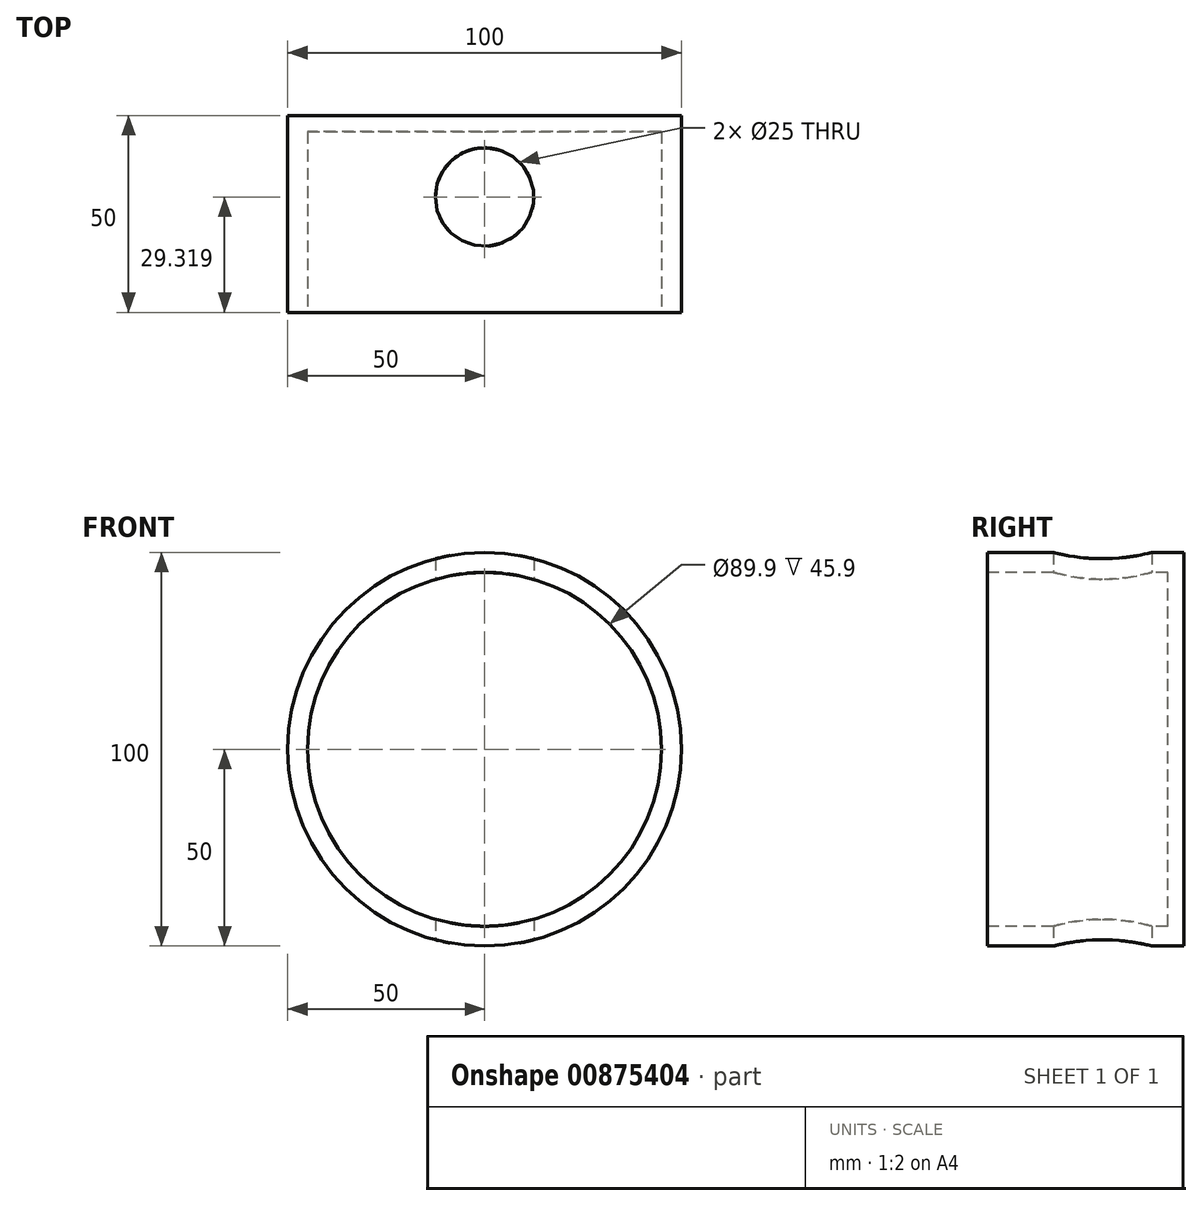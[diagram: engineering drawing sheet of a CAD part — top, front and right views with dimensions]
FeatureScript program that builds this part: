
annotation { "Feature Type Name" : "Feature", "Feature Type Description" : "" }
export const myFeature = defineFeature(function(context is Context, id is Id, definition is map)
    precondition{}
    {
        {
            var Q0;
            Q0=qCreatedBy(makeId("Front.planeOp"),FACE);
            var sketch = newSketch(context, id + "F0", { "sketchPlane" : qUnion([Q0])});
            skCircle(sketch, "E0", {"center": v(0, 0) * mm, "radius": 50 * mm});
            skSolve(sketch);
        }
        {
            var Q0;
            Q0 = qSketchRegion(id + "F0", true);
            extrude(context, id + "F1", {"entities" : qUnion([Q0]), "oppositeDirection" : true, "depth" : 50 * mm, "offsetDistance" : 25 * mm});
        }
        {
            var Q0;
            Q0=qCreatedBy(makeId("Top.planeOp"),FACE);
            var sketch = newSketch(context, id + "F2", { "sketchPlane" : qUnion([Q0])});
            skCircle(sketch, "E1", {"center": v(0, 29.32) * mm, "radius": 12.5 * mm});
            skSolve(sketch);
        }
        {
            var Q0;
            Q0 = qSketchRegion(id + "F2", true);
            extrude(context, id + "F3", {"entities" : qUnion([Q0]), "operationType" : NewBodyOperationType.REMOVE, "endBound" : BoundingType.SYMMETRIC, "depth" : 208.4 * mm, "offsetDistance" : 25 * mm});
        }
        {
            var Q0;
            Q0=qCreatedBy(makeId("Front.planeOp"),FACE);
            var sketch = newSketch(context, id + "F4", { "sketchPlane" : qUnion([Q0])});
            skCircle(sketch, "E2", {"center": v(0, 0) * mm, "radius": 44.95 * mm});
            skSolve(sketch);
        }
        {
            var Q0;
            Q0=makeQuery(id+"F4.imprint","IMPRINT",FACE,{"disambiguationData":[TD([[makeQuery(id+"F4.imprint","IMPRINT",EDGE,{"derivedFrom":sQuery(id+"F4.wireOp",EDGE,"E2")}),1.0]])]});
            extrude(context, id + "F5", {"entities" : qUnion([Q0]), "operationType" : NewBodyOperationType.REMOVE, "oppositeDirection" : true, "depth" : 45.9 * mm, "offsetDistance" : 25 * mm});
        }
    });
